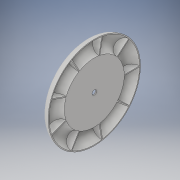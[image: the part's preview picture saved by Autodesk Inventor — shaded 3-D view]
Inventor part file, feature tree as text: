
AUTODESK INVENTOR PART (.ipt)
format: ipt  version: 2019 (Build 230136000, 136)  size: 504,320 bytes
history: native  units: mm
features: sketch x2, other x1, revolve x1, extrude x1, pattern_circular x1
ambient origin geometry x8: Origin, YZ Plane, XZ Plane, XY Plane, X Axis, Y Axis, Z Axis, Center Point
bodies: Body1 (feature_tree)
feature tree (6):
  other  "Твердое тело1"
  revolve  "Вращение1"
  extrude  "Выдавливание1"  Depth=3.0mm
  pattern_circular  "Круговой массив1"  Angle=90.0deg  [1 undecoded]
  sketch  "Эскиз1"
  sketch  "Эскиз2"
note: 1 required parameter value undecoded (feature->parameter linkage not recoverable at this tier; creation-order binding heuristic only, values carry confidence <= 0.55)
